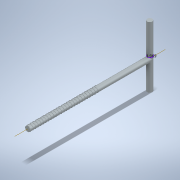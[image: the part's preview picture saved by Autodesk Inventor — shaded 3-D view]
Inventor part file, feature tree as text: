
AUTODESK INVENTOR PART (.ipt)
format: ipt  version: 2020 (Build 240168000, 168)  size: 619,520 bytes
history: native  units: in
note: dims shown in document units (in); Inventor stores cm internally (conversion verified against a paired STEP export)
features: sketch x3, extrude x2, other x2, helix x1, plane x1
ambient origin geometry x8: Origin, YZ Plane, XZ Plane, XY Plane, X Axis, Y Axis, Z Axis, Center Point
bodies: Solid1 (feature_tree)
feature tree (9):
  extrude  "Extrusion1"  Depth=47.2441in TaperAngle=0.0deg
  sketch  "Sketch2"  dims[d4=1.0in d5=1.0in d6=10.5996in d7=0.0in d8=90.0deg d9=90.0deg d10=0.0in d11=0.0in d12=0.9843in]
  other  "Work Axis1"
  helix  "Coil1"  [1 undecoded]
  plane  "Work Plane1"
  sketch  "Sketch3"  dims[d13=1.9685in d14=23.622in d15=0.0in]
  extrude  "Extrusion2"  Depth=0.9843in
  other  "Work Axis2"
  sketch  "Sketch1"  dims[d0=1.9685in d1=47.2441in d2=0.0in d3=0.1969in]
note: 1 required parameter value undecoded (feature->parameter linkage not recoverable at this tier; creation-order binding heuristic only, values carry confidence <= 0.55)
